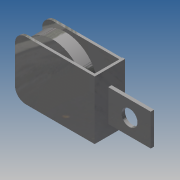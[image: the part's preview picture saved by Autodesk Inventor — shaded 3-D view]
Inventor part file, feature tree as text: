
AUTODESK INVENTOR PART (.ipt)
format: ipt  version: 2014 SP1 (Build 180222100, 222)  size: 184,832 bytes
history: native  units: in
note: dims shown in document units (in); Inventor stores cm internally (conversion verified against a paired STEP export)
features: extrude x6, sketch x6, plane x1, mirror x1
ambient origin geometry x8: Origin, YZ Plane, XZ Plane, XY Plane, X Axis, Y Axis, Z Axis, Center Point
bodies: Solid1 (feature_tree)
feature tree (14):
  extrude  "wheel"  Depth=0.3in TaperAngle=0.0deg
  extrude  "axle"  Depth=0.2in TaperAngle=0.0deg
  extrude  "side"  Depth=0.25in
  plane  "Work Plane1"
  mirror  "Mirror1"
  extrude  "Extrusion4"  Depth=0.06in TaperAngle=0.0deg
  extrude  "Extrusion5"  Depth=0.5in
  extrude  "Extrusion6"  [1 undecoded]
  sketch  "Sketch1"  dims[d0=1.5in d2=0.3in d3=0.0in]
  sketch  "Sketch2"  dims[d4=0.3in d7=0.2in d8=0.5in d9=0.0in d10=0.0in]
  sketch  "Sketch3"  dims[d11=0.06in d12=0.0in d13=0.25in]
  sketch  "Sketch4"  dims[d14=-0.35in d15=0.06in d16=0.0in]
  sketch  "Sketch5"  dims[d17=1.0in d18=0.0in d19=0.5in]
  sketch  "Sketch6"  dims[d20=1.0in d21=0.0in]
note: 1 required parameter value undecoded (feature->parameter linkage not recoverable at this tier; creation-order binding heuristic only, values carry confidence <= 0.55)
